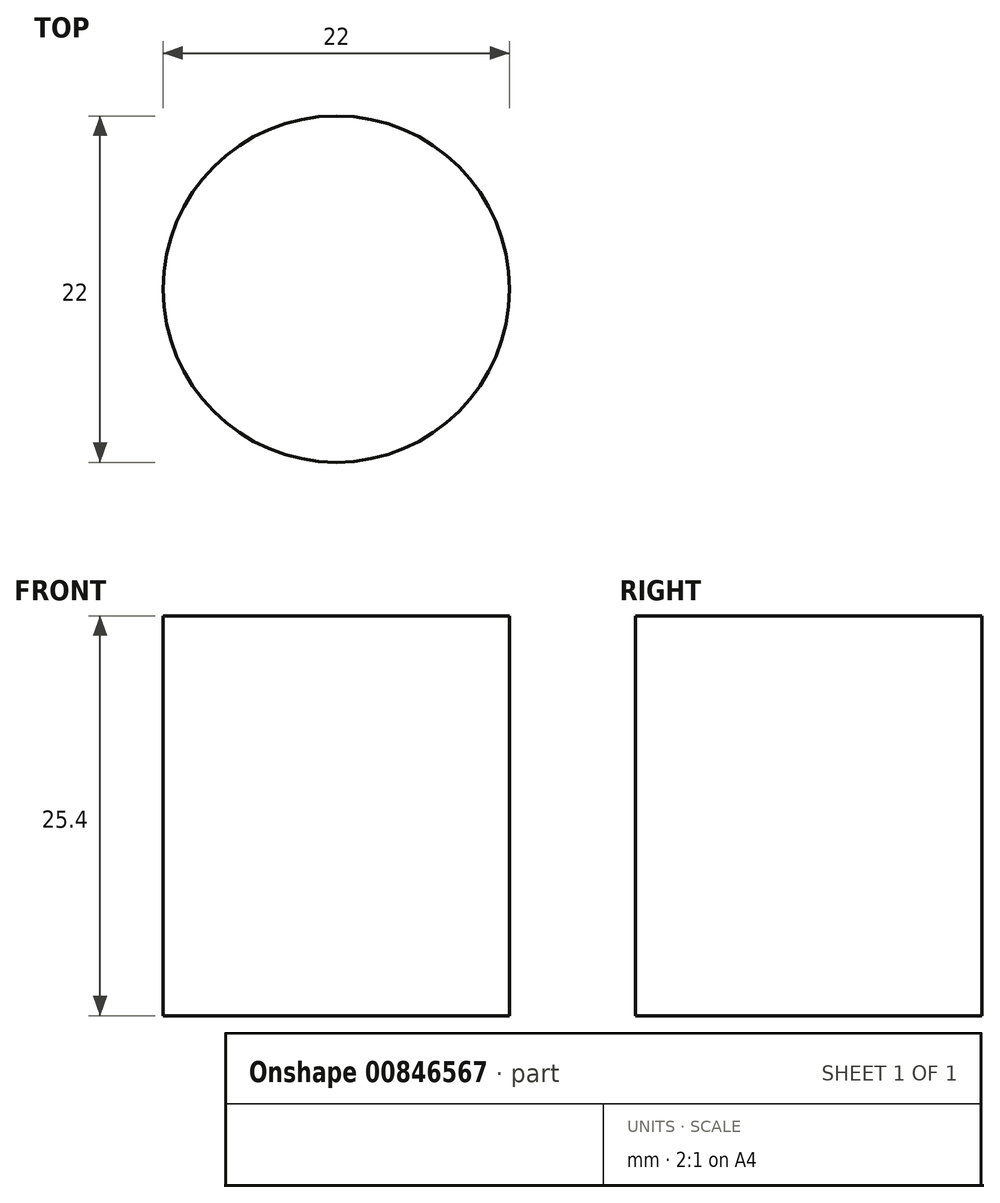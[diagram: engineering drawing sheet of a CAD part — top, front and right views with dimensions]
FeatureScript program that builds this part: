
annotation { "Feature Type Name" : "Feature", "Feature Type Description" : "" }
export const myFeature = defineFeature(function(context is Context, id is Id, definition is map)
    precondition{}
    {
        {
            var Q0;
            Q0=qCreatedBy(makeId("Top.planeOp"),FACE);
            var sketch = newSketch(context, id + "F0", { "sketchPlane" : qUnion([Q0])});
            skCircle(sketch, "E0", {"center": v(0, 0) * mm, "radius": 11 * mm});
            skSolve(sketch);
        }
        {
            var Q0;
            Q0 = qSketchRegion(id + "F0", true);
            extrude(context, id + "F1", {"entities" : qUnion([Q0]), "depth" : 25.4 * mm, "offsetDistance" : 25.4 * mm});
        }
    });
